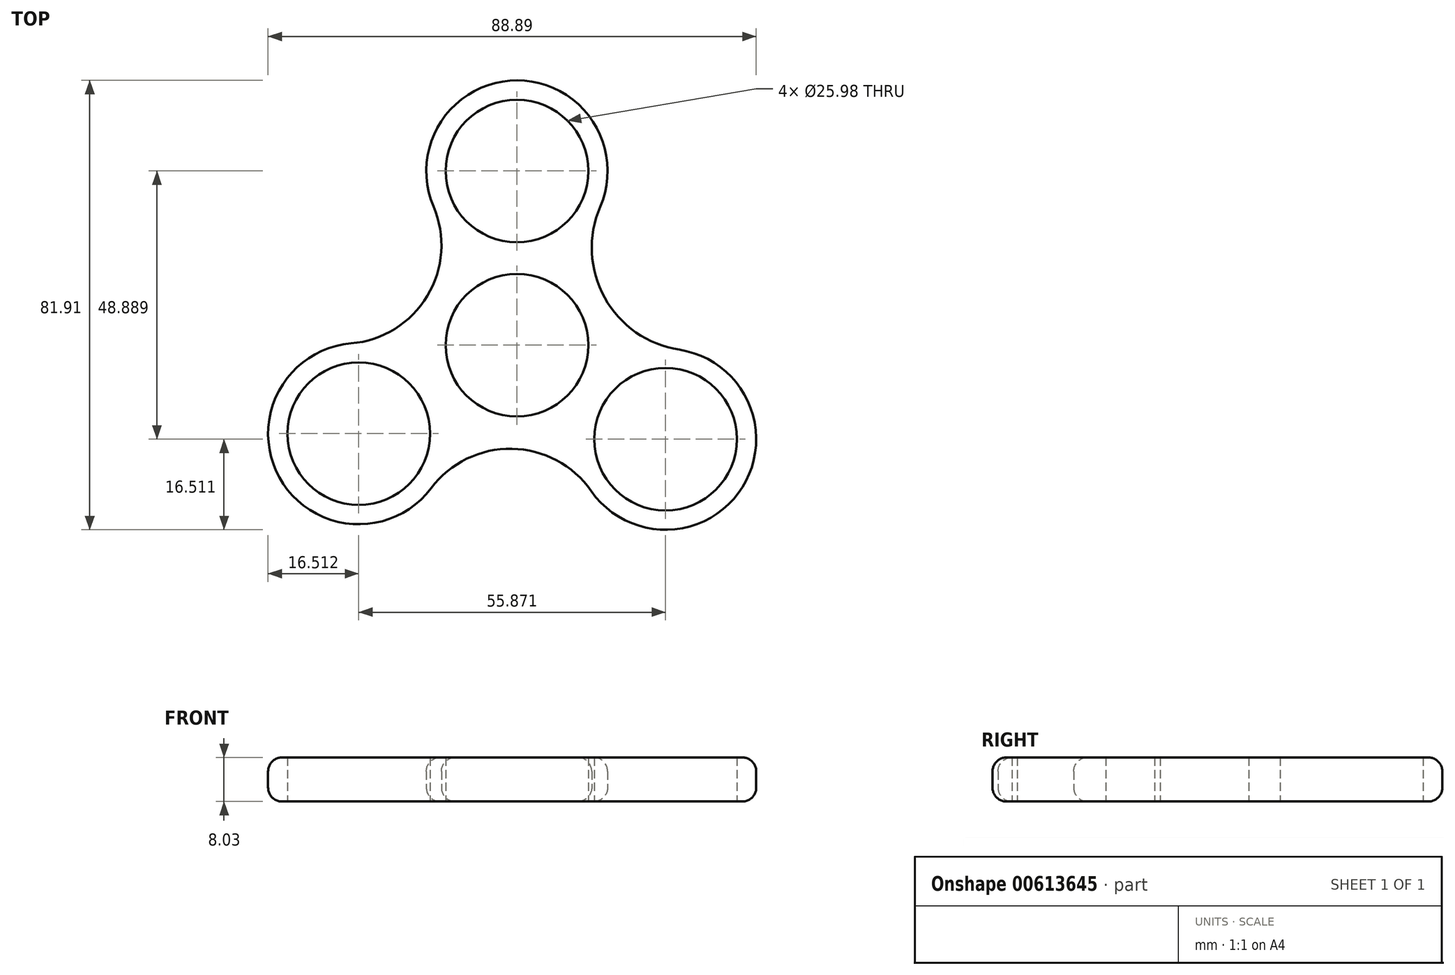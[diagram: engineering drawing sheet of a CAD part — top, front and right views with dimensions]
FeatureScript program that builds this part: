
annotation { "Feature Type Name" : "Feature", "Feature Type Description" : "" }
export const myFeature = defineFeature(function(context is Context, id is Id, definition is map)
    precondition{}
    {
        {
            var Q0;
            Q0=qCreatedBy(makeId("Top.planeOp"),FACE);
            var sketch = newSketch(context, id + "F0", { "sketchPlane" : qUnion([Q0])});
            skCircle(sketch, "E0", {"center": v(0, 0) * mm, "radius": 13 * mm});
            skLineSegment(sketch, "E1.1", {"start": v(-42.37, -16.16) * mm, "end": v(-42.02, -15.55) * mm});
            skLineSegment(sketch, "E1.3", {"start": v(-15.6, -15.5) * mm, "end": v(-15.24, -16.1) * mm});
            skArc(sketch, "E2", {"start": v(-30.2, 0.32) * mm, "mid": v(-16.33, 8.97) * mm, "end": v(-15.2, 25.28) * mm});
            skArc(sketch, "E3", {"start": v(13.52, -26.58) * mm, "mid": v(-0.91, -18.88) * mm, "end": v(-15.61, -26.05) * mm});
            skArc(sketch, "E4", {"start": v(15.16, 25.21) * mm, "mid": v(15.98, 8.66) * mm, "end": v(29.57, -0.82) * mm});
            skPoint(sketch, "E4.startSnap0", {"position": v(9.9, 25.21) * mm});
            skArc(sketch, "E5", {"start": v(-30.2, 0.32) * mm, "mid": v(-43.25, -24.13) * mm, "end": v(-15.61, -26.05) * mm});
            skArc(sketch, "E6", {"start": v(13.52, -26.58) * mm, "mid": v(41.07, -25.87) * mm, "end": v(29.57, -0.82) * mm});
            skArc(sketch, "E7", {"start": v(15.16, 25.21) * mm, "mid": v(0.04, 48.26) * mm, "end": v(-15.2, 25.28) * mm});
            skCircle(sketch, "E8", {"center": v(0, 31.75) * mm, "radius": 13 * mm});
            skCircle(sketch, "E9", {"center": v(27.06, -17.14) * mm, "radius": 13 * mm});
            skCircle(sketch, "E10", {"center": v(-28.8, -16.13) * mm, "radius": 13 * mm});
            skSolve(sketch);
        }
        {
            var Q0;
            Q0=qSketchRegion(id+"F0",true);
            extrude(context, id + "F1", {"entities" : qUnion([Q0]), "depth" : 8.03 * mm, "offsetDistance" : 25.4 * mm});
        }
        {
            var Q0;
            Q0=makeQuery(id+"F1.opExtrude","CAP_EDGE",EDGE,{"disambiguationData":[OSD([sQuery(id+"F0.wireOp",EDGE,"E3")])],"isStart":false});
            var Q1;
            Q1=makeQuery(id+"F1.opExtrude","CAP_EDGE",EDGE,{"disambiguationData":[OSD([sQuery(id+"F0.wireOp",EDGE,"E5")])],"isStart":false});
            var Q2;
            Q2=makeQuery(id+"F1.opExtrude","CAP_EDGE",EDGE,{"disambiguationData":[OSD([sQuery(id+"F0.wireOp",EDGE,"E2")])],"isStart":false});
            var Q3;
            Q3=makeQuery(id+"F1.opExtrude","CAP_EDGE",EDGE,{"disambiguationData":[OSD([sQuery(id+"F0.wireOp",EDGE,"E7")])],"isStart":false});
            var Q4;
            Q4=makeQuery(id+"F1.opExtrude","CAP_EDGE",EDGE,{"disambiguationData":[OSD([sQuery(id+"F0.wireOp",EDGE,"E4")])],"isStart":false});
            var Q5;
            Q5=makeQuery(id+"F1.opExtrude","CAP_EDGE",EDGE,{"disambiguationData":[OSD([sQuery(id+"F0.wireOp",EDGE,"E6")])],"isStart":false});
            fillet(context, id + "F2", {"entities" : qUnion([Q0, Q1, Q2, Q3, Q4, Q5]), "radius" : 2.54 * mm, "tangentPropagation" : true, "allowEdgeOverflow" : false});
        }
        {
            var Q0;
            Q0=makeQuery(id+"F1.opExtrude","CAP_EDGE",EDGE,{"disambiguationData":[OSD([sQuery(id+"F0.wireOp",EDGE,"E2")])],"isStart":true});
            var Q1;
            Q1=makeQuery(id+"F1.opExtrude","CAP_EDGE",EDGE,{"disambiguationData":[OSD([sQuery(id+"F0.wireOp",EDGE,"E5")])],"isStart":true});
            var Q2;
            Q2=makeQuery(id+"F1.opExtrude","CAP_EDGE",EDGE,{"disambiguationData":[OSD([sQuery(id+"F0.wireOp",EDGE,"E3")])],"isStart":true});
            var Q3;
            Q3=makeQuery(id+"F1.opExtrude","CAP_EDGE",EDGE,{"disambiguationData":[OSD([sQuery(id+"F0.wireOp",EDGE,"E4")])],"isStart":true});
            var Q4;
            Q4=makeQuery(id+"F1.opExtrude","CAP_EDGE",EDGE,{"disambiguationData":[OSD([sQuery(id+"F0.wireOp",EDGE,"E6")])],"isStart":true});
            var Q5;
            Q5=makeQuery(id+"F1.opExtrude","CAP_EDGE",EDGE,{"disambiguationData":[OSD([sQuery(id+"F0.wireOp",EDGE,"E7")])],"isStart":true});
            fillet(context, id + "F3", {"entities" : qUnion([Q0, Q1, Q2, Q3, Q4, Q5]), "radius" : 2.54 * mm, "tangentPropagation" : true, "allowEdgeOverflow" : false});
        }
    });
